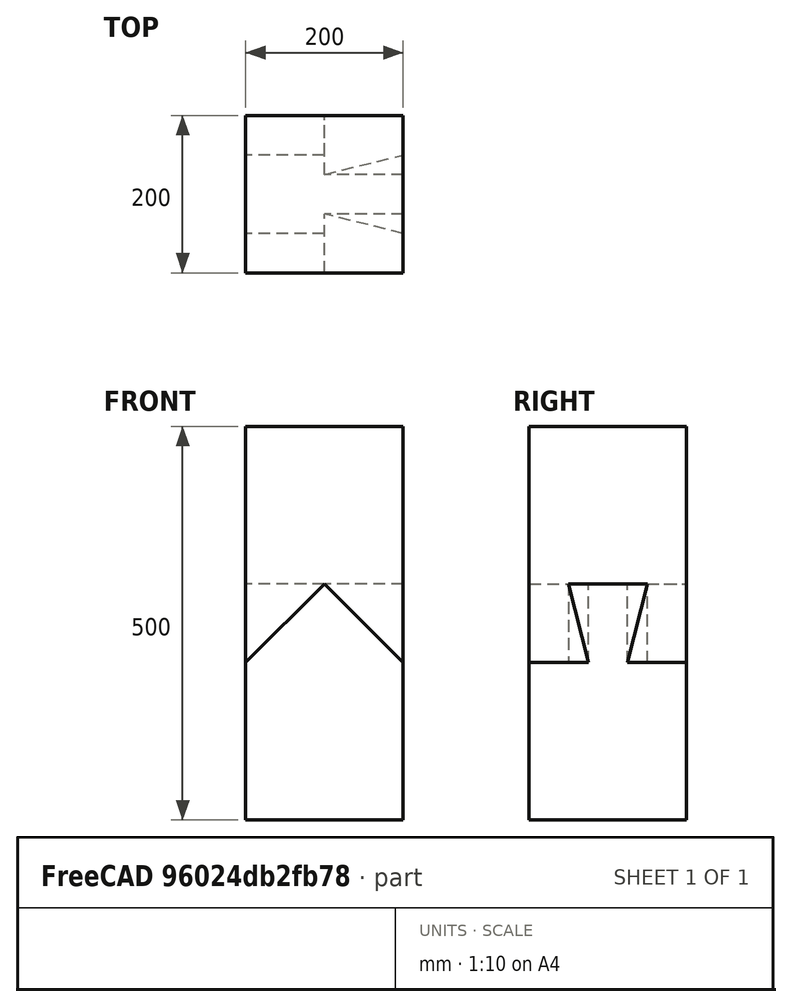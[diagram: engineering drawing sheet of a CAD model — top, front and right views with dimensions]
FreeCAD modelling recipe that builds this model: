
FCSTD DOCUMENT  (FreeCAD 0.19R16207 (Git))
Label: EMENDA 5
License: All rights reserved
LicenseURL: http://en.wikipedia.org/wiki/All_rights_reserved
objects: Part::Feature×14, Part::Line×9, Part::Box×3, Part::Chamfer×1, Part::MultiFuse×1, Part::Cut×1
note: 29 computed .brp shape members not serialized (recipe doc carries the construction recipe); baked Part::Feature solids carry a one-line shape summary decoded from their .brp

FEATURE [Part::Line] Line
  AttacherType = Attacher::AttachEngine3D
  X1 = 0
  X2 = 0
  Y1 = -25
  Y2 = 25
  Z1 = 0
  Z2 = 0
FEATURE [Part::Line] Line001
  AttacherType = Attacher::AttachEngine3D
  X1 = 100
  X2 = 100
  Y1 = -50
  Y2 = 50
  Z1 = 0
  Z2 = 0
FEATURE [Part::Line] Line002
  AttacherType = Attacher::AttachEngine3D
  X1 = 0
  X2 = 100
  Y1 = -25
  Y2 = -50
  Z1 = 0
  Z2 = 0
FEATURE [Part::Line] Line003
  AttacherType = Attacher::AttachEngine3D
  X1 = 0
  X2 = 100
  Y1 = 25
  Y2 = 50
  Z1 = 0
  Z2 = 0
FEATURE [Part::Line] Line004
  AttacherType = Attacher::AttachEngine3D
  X1 = 100
  X2 = 100
  Y1 = -50
  Y2 = -25
  Z1 = 0
  Z2 = -100
FEATURE [Part::Line] Line005
  AttacherType = Attacher::AttachEngine3D
  X1 = 100
  X2 = 100
  Y1 = 50
  Y2 = 25
  Z1 = 0
  Z2 = -100
FEATURE [Part::Line] Line006
  AttacherType = Attacher::AttachEngine3D
  X1 = 100
  X2 = 100
  Y1 = 25
  Y2 = -25
  Z1 = -100
  Z2 = -100
FEATURE [Part::Line] Line007
  AttacherType = Attacher::AttachEngine3D
  X1 = 0
  X2 = 100
  Y1 = -25
  Y2 = -25
  Z1 = 0
  Z2 = -100
FEATURE [Part::Line] Line008
  AttacherType = Attacher::AttachEngine3D
  X1 = 0
  X2 = 100
  Y1 = 25
  Y2 = 25
  Z1 = 0
  Z2 = -100
FEATURE [Part::Feature] Wire
  shape: bbox 100 x 100 x 2e-07 mm, 0 faces, 0 solids (baked)
FEATURE [Part::Feature] Wire001
  shape: bbox 100 x 50 x 100 mm, 0 faces, 0 solids (baked)
FEATURE [Part::Feature] Wire002
  shape: bbox 100 x 25 x 100 mm, 0 faces, 0 solids (baked)
FEATURE [Part::Feature] Wire003
  shape: bbox 100 x 25 x 100 mm, 0 faces, 0 solids (baked)
FEATURE [Part::Feature] Wire004
  shape: bbox 2e-07 x 100 x 100 mm, 0 faces, 0 solids (baked)
FEATURE [Part::Feature] Face
  shape: bbox 110 x 110 x 2e-07 mm, 1 faces, 0 solids (baked)
FEATURE [Part::Feature] Face001
  shape: bbox 165 x 27.5 x 165 mm, 1 faces, 0 solids (baked)
FEATURE [Part::Feature] Face002
  shape: bbox 110 x 55 x 110 mm, 1 faces, 0 solids (baked)
FEATURE [Part::Feature] Face003
  shape: bbox 165 x 27.5 x 165 mm, 1 faces, 0 solids (baked)
FEATURE [Part::Feature] Face004
  shape: bbox 2e-07 x 110 x 110 mm, 1 faces, 0 solids (baked)
FEATURE [Part::Feature] Shell
  shape: bbox 165 x 110 x 165 mm, 5 faces, 0 solids (baked)
FEATURE [Part::Feature] Solid
  shape: bbox 165 x 110 x 165 mm, 5 faces (baked)
FEATURE [Part::Box] Box  label="Cube"
  AttacherType = Attacher::AttachEngine3D
  Height = 100
  Length = 100
  Placement = pos=(0,-50,0) rot=(0,1,0;3.14159rad)
  Width = 100
FEATURE [Part::Box] Box001  label="Cube001"
  AttacherType = Attacher::AttachEngine3D
  Height = 300
  Length = 200
  Placement = pos=(100,-100,1.22e-14) rot=(0,1,0;3.14159rad)
  Width = 200
FEATURE [Part::Chamfer] Chamfer
  Base = -> Box001
  Edges = 2 edges r=99.99: [Edge4,Edge8]
FEATURE [Part::MultiFuse] Fusion
  Shapes = -> [Chamfer,Box,Solid]
FEATURE [Part::Feature] Fusion001
  shape: bbox 258.3 x 200 x 358.3 mm, 16 faces (baked)
FEATURE [Part::Box] Box002  label="Cube002"
  AttacherType = Attacher::AttachEngine3D
  Height = 300
  Length = 200
  Placement = pos=(-100,-100,-100) rot=(0,0,1;0rad)
  Width = 200
FEATURE [Part::Cut] Cut
  Base = -> Box002
  Tool = -> Fusion001
FEATURE [Part::Feature] Fusion002
  shape: bbox 258.3 x 200 x 358.3 mm, 16 faces (baked)
